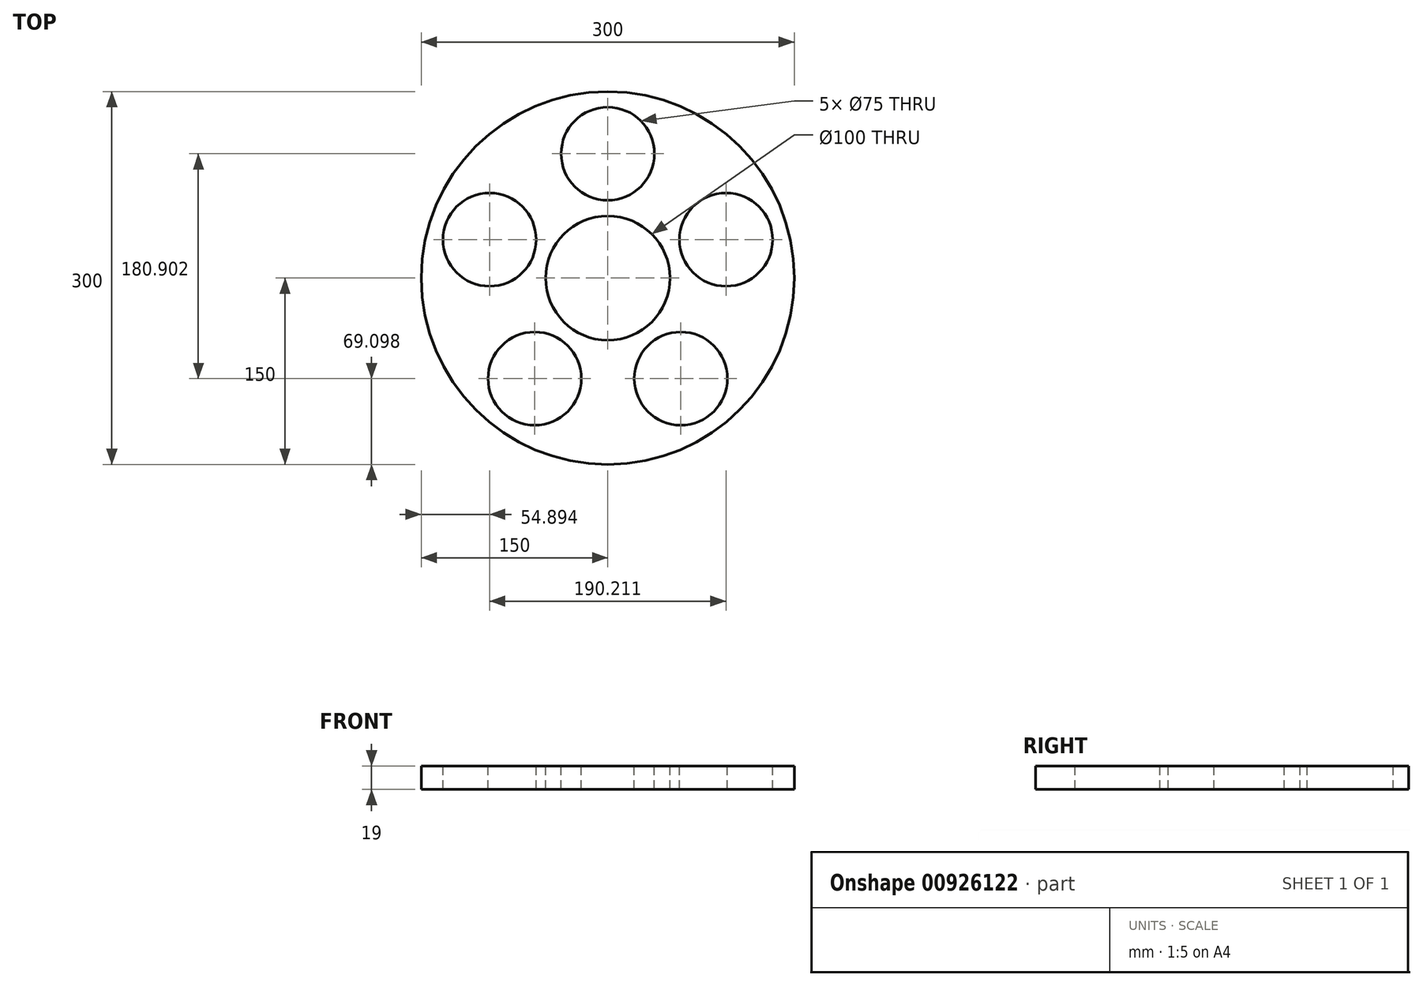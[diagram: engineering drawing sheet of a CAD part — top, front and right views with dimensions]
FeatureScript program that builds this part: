
annotation { "Feature Type Name" : "Feature", "Feature Type Description" : "" }
export const myFeature = defineFeature(function(context is Context, id is Id, definition is map)
    precondition{}
    {
        {
            var Q0;
            Q0=qCreatedBy(makeId("Top.planeOp"),FACE);
            var sketch = newSketch(context, id + "F0", { "sketchPlane" : qUnion([Q0])});
            skCircle(sketch, "E0", {"center": v(0, 0) * mm, "radius": 150 * mm});
            skSolve(sketch);
        }
        {
            var Q0;
            Q0 = qSketchRegion(id + "F0", true);
            extrude(context, id + "F1", {"entities" : qUnion([Q0]), "depth" : 19 * mm, "offsetDistance" : 25 * mm});
        }
        {
            var Q0;
            Q0=makeQuery(id+"F1.opExtrude","CAP_FACE",FACE,{"disambiguationData":[OSD([sQuery(id+"F0.wireOp",EDGE,"E0")])],"isStart":false});
            var sketch = newSketch(context, id + "F2", { "sketchPlane" : qUnion([Q0])});
            skCircle(sketch, "E1", {"center": v(0, 0) * mm, "radius": 50 * mm});
            skCircle(sketch, "E2", {"center": v(0, 100) * mm, "radius": 37.5 * mm});
            skCircle(sketch, "E3.1.0", {"center": v(-95.1, 30.9) * mm, "radius": 37.5 * mm});
            skCircle(sketch, "E3.2.0", {"center": v(-58.78, -80.9) * mm, "radius": 37.5 * mm});
            skCircle(sketch, "E3.3.0", {"center": v(58.78, -80.9) * mm, "radius": 37.5 * mm});
            skCircle(sketch, "E3.4.0", {"center": v(95.1, 30.9) * mm, "radius": 37.5 * mm});
            skSolve(sketch);
        }
        {
            var Q0;
            Q0 = qSketchRegion(id + "F2", true);
            extrude(context, id + "F3", {"entities" : qUnion([Q0]), "operationType" : NewBodyOperationType.REMOVE, "oppositeDirection" : true, "depth" : 53 * mm, "offsetDistance" : 25 * mm});
        }
    });
